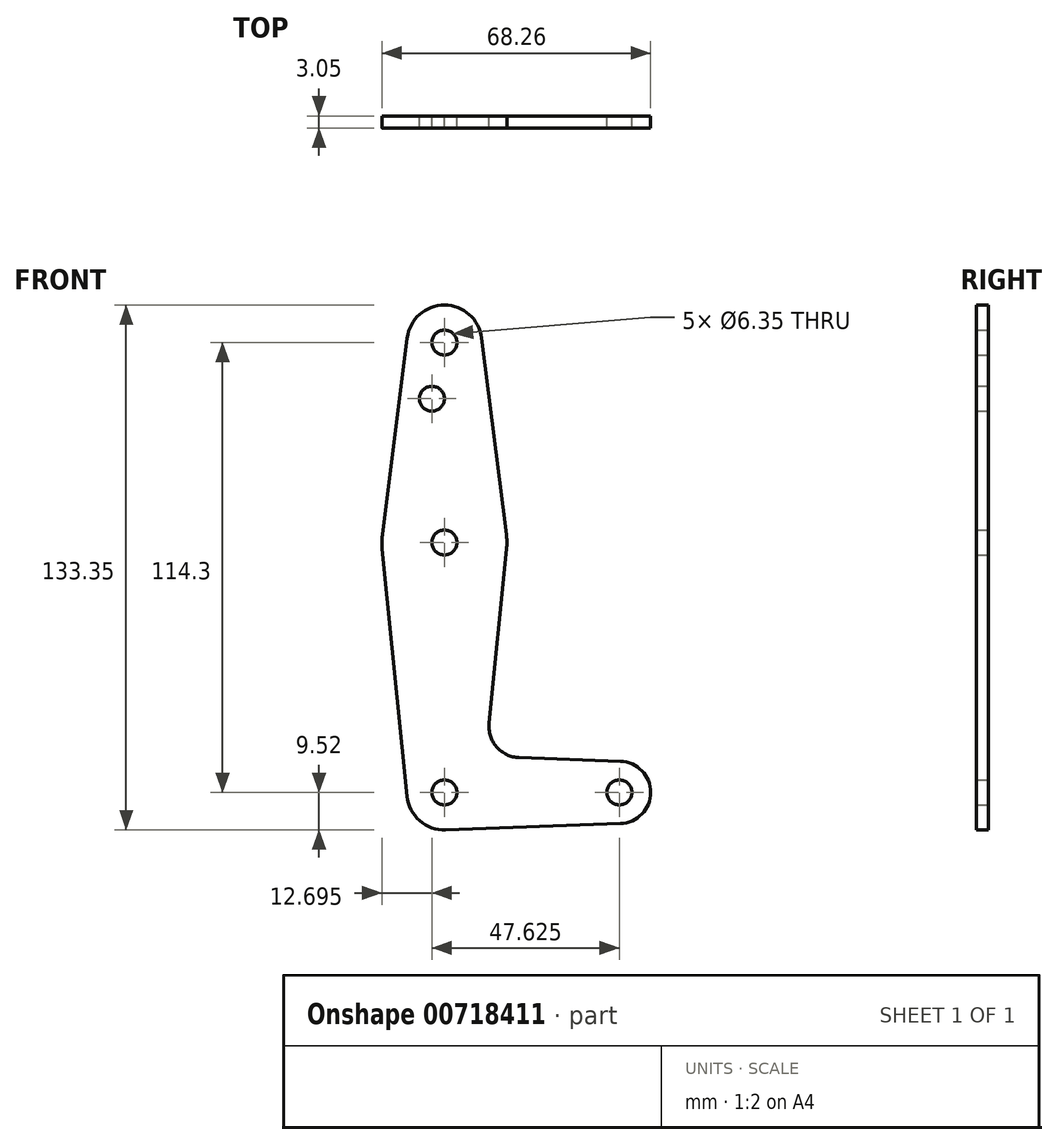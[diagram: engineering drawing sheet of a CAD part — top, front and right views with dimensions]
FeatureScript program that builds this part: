
annotation { "Feature Type Name" : "Feature", "Feature Type Description" : "" }
export const myFeature = defineFeature(function(context is Context, id is Id, definition is map)
    precondition{}
    {
        {
            var Q0;
            Q0=qCreatedBy(makeId("Front.planeOp"),FACE);
            var sketch = newSketch(context, id + "F0", { "sketchPlane" : qUnion([Q0])});
            skLineSegment(sketch, "E0", {"start": v(0, 0) * mm, "end": v(0, 114.3) * mm, "construction": true});
            skLineSegment(sketch, "E1", {"start": v(0, 0) * mm, "end": v(44.45, 0) * mm, "construction": true});
            skCircle(sketch, "E2", {"center": v(0, 114.3) * mm, "radius": 9.53 * mm});
            skCircle(sketch, "E3", {"center": v(0, 63.5) * mm, "radius": 15.88 * mm});
            skCircle(sketch, "E4", {"center": v(0, 0) * mm, "radius": 9.53 * mm});
            skCircle(sketch, "E5", {"center": v(44.45, 0) * mm, "radius": 7.94 * mm});
            skLineSegment(sketch, "E6", {"start": v(-15.75, 65.48) * mm, "end": v(-9.45, 115.5) * mm});
            skLineSegment(sketch, "E7", {"start": v(9.45, 115.5) * mm, "end": v(15.75, 65.48) * mm});
            skLineSegment(sketch, "E8", {"start": v(-15.8, 61.91) * mm, "end": v(-9.48, -0.95) * mm});
            skLineSegment(sketch, "E9", {"start": v(15.8, 61.91) * mm, "end": v(11.34, 17.6) * mm});
            skLineSegment(sketch, "E10", {"start": v(18.97, 8.85) * mm, "end": v(44.73, 7.93) * mm});
            skLineSegment(sketch, "E11", {"start": v(0.34, -9.52) * mm, "end": v(44.73, -7.93) * mm});
            skArc(sketch, "E12.filletArc", {"start": v(11.34, 17.6) * mm, "mid": v(13.26, 11.57) * mm, "end": v(18.97, 8.85) * mm});
            skCircle(sketch, "E13", {"center": v(0, 114.3) * mm, "radius": 3.18 * mm});
            skCircle(sketch, "E14", {"center": v(-3.18, 100.03) * mm, "radius": 3.18 * mm});
            skCircle(sketch, "E15", {"center": v(0, 63.5) * mm, "radius": 3.18 * mm});
            skCircle(sketch, "E16", {"center": v(0, 0) * mm, "radius": 3.18 * mm});
            skCircle(sketch, "E17", {"center": v(44.45, 0) * mm, "radius": 3.18 * mm});
            skSolve(sketch);
        }
        {
            var Q0;
            Q0=makeQuery(id+"F0.imprint","IMPRINT",FACE,{"disambiguationData":[TD([[makeQuery(id+"F0.imprint","IMPRINT",EDGE,{"derivedFrom":sQuery(id+"F0.wireOp",EDGE,"E13")}),-1.0]])]});
            var Q1;
            Q1=makeQuery(id+"F0.imprint","IMPRINT",FACE,{"disambiguationData":[TD([[makeQuery(id+"F0.imprint","IMPRINT",EDGE,{"derivedFrom":sQuery(id+"F0.wireOp",EDGE,"E16")}),-1.0]])]});
            var Q2;
            Q2=makeQuery(id+"F0.imprint","IMPRINT",FACE,{"disambiguationData":[TD([[makeQuery(id+"F0.imprint","IMPRINT",EDGE,{"derivedFrom":sQuery(id+"F0.wireOp",EDGE,"E17")}),-1.0]])]});
            var Q3;
            Q3=makeQuery(id+"F0.imprint","IMPRINT",FACE,{"disambiguationData":[TD([[makeQuery(id+"F0.imprint","IMPRINT",EDGE,{"derivedFrom":sQuery(id+"F0.wireOp",EDGE,"E15")}),-1.0]])]});
            var Q4;
            {var subQ0=sQuery(id+"F0.wireOp",EDGE,"E6");Q4=makeQuery(id+"F0.imprint","IMPRINT",FACE,{"disambiguationData":[TD([[makeQuery(id+"F0.imprint","IMPRINT",EDGE,{"derivedFrom":subQ0}),-1.0]])]});}
            var Q5;
            {var subQ3=sQuery(id+"F0.wireOp",EDGE,"E8");Q5=makeQuery(id+"F0.imprint","IMPRINT",FACE,{"disambiguationData":[TD([[makeQuery(id+"F0.imprint","IMPRINT",EDGE,{"derivedFrom":subQ3}),1.0]])]});}
            extrude(context, id + "F1", {"entities" : qUnion([Q0, Q1, Q2, Q3, Q4, Q5]), "depth" : 3.05 * mm, "offsetDistance" : 25.4 * mm});
        }
    });
